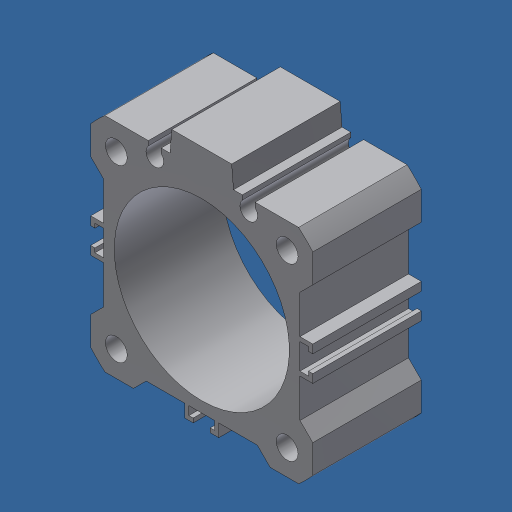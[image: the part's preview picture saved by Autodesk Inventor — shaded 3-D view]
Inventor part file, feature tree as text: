
AUTODESK INVENTOR PART (.ipt)
format: ipt  version: 2024.3 (Build 283343000, 343)  size: 233,472 bytes
history: native  units: mm (DEFAULTED — no unit token found)
features: other x1, sketch x1, extrude x1, hole x1
ambient origin geometry x8: Origin, YZ Plane, XZ Plane, XY Plane, X Axis, Y Axis, Z Axis, Center Point
bodies: Body1 (feature_tree)
feature tree (4):
  other  "Finish - None"
  sketch  "Sketch1"  dims[d3=7.437443mm d4=7.0mm d6=31.0mm d7=5.0mm d8=3.0mm d9=2.075mm d10=2.5mm d11=11.0mm d12=69.0mm d13=26.0mm d15=34.5mm d16=34.5mm d17=26.0mm d18=23.0mm d19=26.0mm d20=13.0mm d21=26.0mm d22=26.0mm d23=6.677081mm d24=23.0mm d25=1.0mm d26=1.0mm d27=26.0mm d28=8.0mm d29=4.0mm d30=4.0mm d31=2.0mm d32=20.5mm d33=40.0mm d34=20.0mm d35=20.0mm d36=25.4mm d37=0.0mm d38=5.1054mm d39=12.7mm d40=9.525mm d41=6.35mm d42=14.3117mm d43=19.05mm d44=20.594885mm]
  extrude  "SMC, 40MM"  Depth=7.0mm
  hole  "Hole1"  [1 undecoded]
note: 1 required parameter value undecoded (feature->parameter linkage not recoverable at this tier; creation-order binding heuristic only, values carry confidence <= 0.55)
